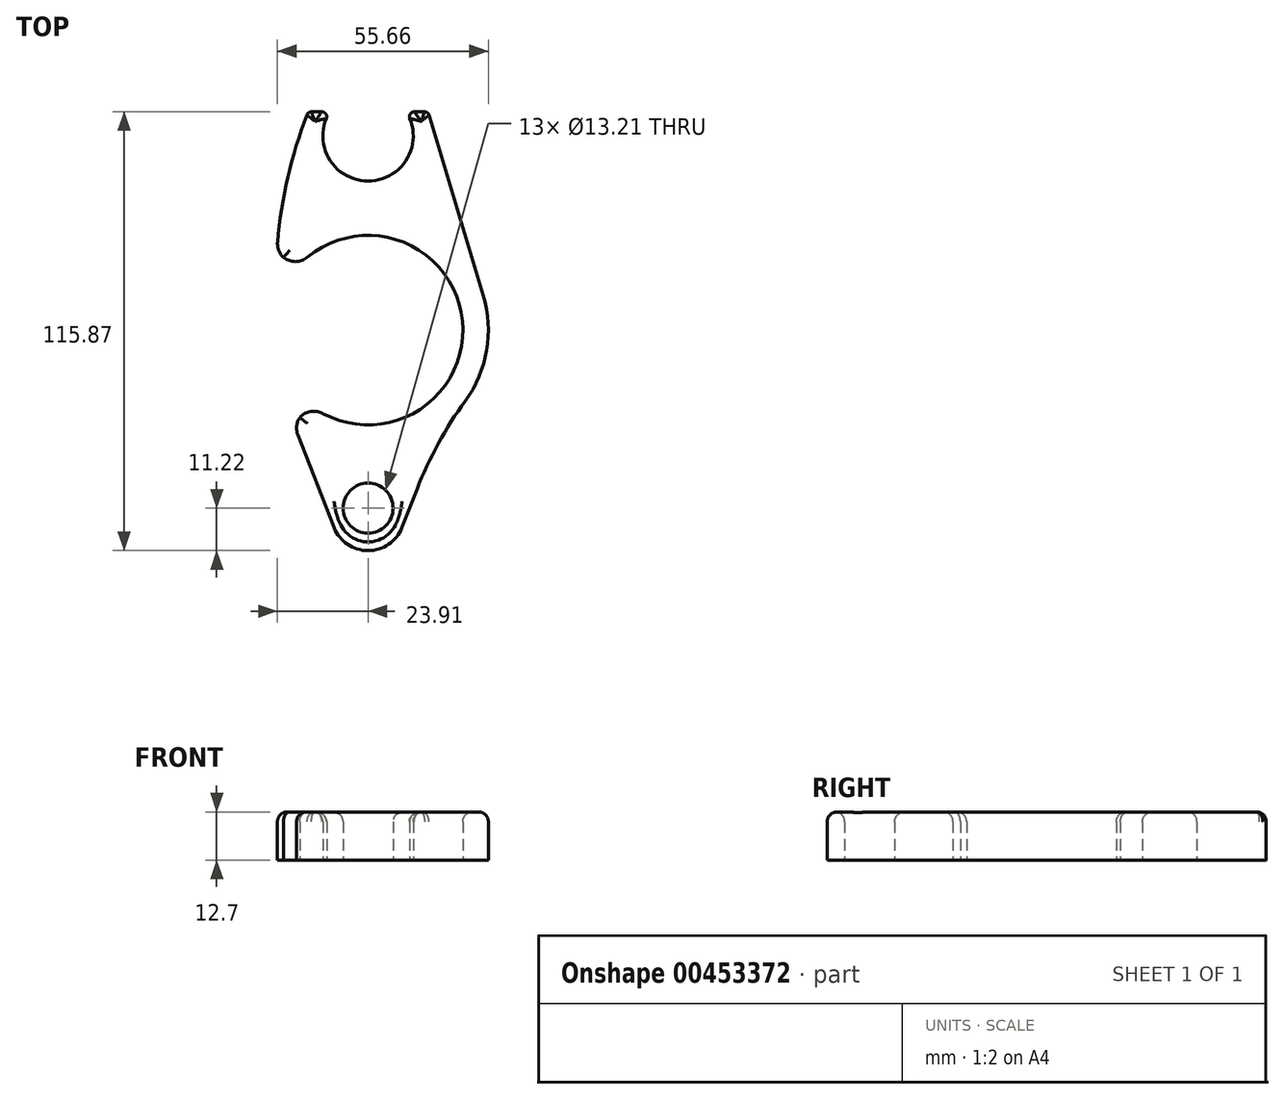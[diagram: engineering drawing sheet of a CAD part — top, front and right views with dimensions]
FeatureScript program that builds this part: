
annotation { "Feature Type Name" : "Feature", "Feature Type Description" : "" }
export const myFeature = defineFeature(function(context is Context, id is Id, definition is map)
    precondition{}
    {
        {
            var Q0;
            Q0=qCreatedBy(makeId("Top.planeOp"),FACE);
            var sketch = newSketch(context, id + "F0", { "sketchPlane" : qUnion([Q0])});
            skCircle(sketch, "E0", {"center": v(0, 0) * mm, "radius": 31.75 * mm});
            skCircle(sketch, "E1", {"center": v(0, -47) * mm, "radius": 6.6 * mm});
            skCircle(sketch, "E2", {"center": v(0, 51.3) * mm, "radius": 11.94 * mm});
            skCircle(sketch, "E3.0", {"center": v(0, 51.3) * mm, "radius": 17.02 * mm});
            skLineSegment(sketch, "E4", {"start": v(0, 57.66) * mm, "end": v(-15.79, 57.66) * mm});
            skLineSegment(sketch, "E5", {"start": v(-15.79, 57.66) * mm, "end": v(-26.07, 32.09) * mm});
            skLineSegment(sketch, "E6", {"start": v(-26.07, 32.09) * mm, "end": v(-22.42, 11.11) * mm});
            skLineSegment(sketch, "E7", {"start": v(0, 0) * mm, "end": v(0, 31.75) * mm, "construction": true});
            skLineSegment(sketch, "E8", {"start": v(0, 0) * mm, "end": v(-31.75, 0) * mm, "construction": true});
            skLineSegment(sketch, "E9", {"start": v(-22.42, -17.72) * mm, "end": v(0, -74.98) * mm});
            skLineSegment(sketch, "E10.MirrorCS", {"start": v(22.42, -17.72) * mm, "end": v(0, -74.98) * mm});
            skCircle(sketch, "E11", {"center": v(0, 0) * mm, "radius": 25.02 * mm});
            skLineSegment(sketch, "E12", {"start": v(16.3, 56.2) * mm, "end": v(30.41, 9.12) * mm});
            skLineSegment(sketch, "E13.MirrorCS", {"start": v(0, 57.66) * mm, "end": v(15.79, 57.66) * mm});
            skSolve(sketch);
        }
        {
            var Q0;
            {var subQ1=sQuery(id+"F0.wireOp",EDGE,"E5");Q0=makeQuery(id+"F0.imprint","IMPRINT",FACE,{"disambiguationData":[TD([[makeQuery(id+"F0.imprint","IMPRINT",EDGE,{"derivedFrom":subQ1}),1.0]])]});}
            var Q1;
            {var subQ0=sQuery(id+"F0.wireOp",EDGE,"E4");var subQ6=sQuery(id+"F0.wireOp",EDGE,"E2");var subQ7=makeQuery(id+"F0.imprint","INTERSECT",VERTEX,{"derivedFrom":[subQ6,subQ0]});Q1=makeQuery(id+"F0.imprint","IMPRINT",FACE,{"disambiguationData":[TD([[makeQuery(id+"F0.imprint","IMPRINT",EDGE,{"disambiguationData":[TD([[subQ7,-1.0]])],"derivedFrom":subQ6}),-1.0]])]});}
            var Q2;
            Q2=makeQuery(id+"F0.imprint","IMPRINT",FACE,{"disambiguationData":[TD([[makeQuery(id+"F0.imprint","IMPRINT",EDGE,{"derivedFrom":sQuery(id+"F0.wireOp",EDGE,"E1")}),-1.0]])]});
            var Q3;
            Q3=makeQuery(id+"F0.imprint","IMPRINT",FACE,{"disambiguationData":[TD([[makeQuery(id+"F0.imprint","IMPRINT",EDGE,{"derivedFrom":sQuery(id+"F0.wireOp",EDGE,"E11")}),-1.0]])]});
            extrude(context, id + "F1", {"entities" : qUnion([Q0, Q1, Q2, Q3]), "depth" : 12.7 * mm});
        }
        {
            var Q0;
            Q0=makeQuery(id+"F1.opExtrude","SWEPT_EDGE",EDGE,{"disambiguationData":[OSD([sQuery(id+"F0.wireOp",EDGE,"E9"),sQuery(id+"F0.wireOp",EDGE,"E10.MirrorCS")])]});
            fillet(context, id + "F2", {"entities" : qUnion([Q0]), "radius" : 9.62 * mm, "tangentPropagation" : true, "allowEdgeOverflow" : false});
        }
        {
            var Q0;
            Q0=makeQuery(id+"F1.opExtrude","CAP_FACE",FACE,{"disambiguationData":[OSD([sQuery(id+"F0.wireOp",EDGE,"E0"),sQuery(id+"F0.wireOp",EDGE,"E1"),sQuery(id+"F0.wireOp",EDGE,"E2"),sQuery(id+"F0.wireOp",EDGE,"E3.0"),sQuery(id+"F0.wireOp",EDGE,"E4"),sQuery(id+"F0.wireOp",EDGE,"E5"),sQuery(id+"F0.wireOp",EDGE,"E6"),sQuery(id+"F0.wireOp",EDGE,"E9"),sQuery(id+"F0.wireOp",EDGE,"E10.MirrorCS"),sQuery(id+"F0.wireOp",EDGE,"E11"),sQuery(id+"F0.wireOp",EDGE,"E12"),sQuery(id+"F0.wireOp",EDGE,"E13.MirrorCS")])],"isStart":false});
            var sketch = newSketch(context, id + "F3", { "sketchPlane" : qUnion([Q0])});
            skLineSegment(sketch, "E14", {"start": v(-24.09, 20.69) * mm, "end": v(0, 0) * mm});
            skLineSegment(sketch, "E15", {"start": v(0, 0) * mm, "end": v(-19.56, -25) * mm});
            skArc(sketch, "E16.0", {"start": v(-24.09, 20.69) * mm, "mid": v(-31.6, -3.13) * mm, "end": v(-19.56, -25) * mm});
            skSolve(sketch);
        }
        {
            var Q0;
            Q0 = qSketchRegion(id + "F3", true);
            extrude(context, id + "F4", {"entities" : qUnion([Q0]), "operationType" : NewBodyOperationType.REMOVE, "endBound" : BoundingType.THROUGH_ALL, "oppositeDirection" : true, "depth" : 25.4 * mm});
        }
        {
            var Q0;
            Q0=makeQuery(id+"F1.opExtrude","SWEPT_EDGE",EDGE,{"disambiguationData":[OSD([sQuery(id+"F0.wireOp",EDGE,"E5"),sQuery(id+"F0.wireOp",EDGE,"E6")])]});
            fillet(context, id + "F5", {"entities" : qUnion([Q0]), "radius" : 121.36 * mm, "tangentPropagation" : true, "allowEdgeOverflow" : false});
        }
        {
            var Q0;
            Q0=makeQuery(id+"F4.boolean.opBoolean","INTERSECT",EDGE,{"derivedFrom":[makeQuery(id+"F1.opExtrude","SWEPT_FACE",FACE,{"disambiguationData":[OSD([sQuery(id+"F0.wireOp",EDGE,"E11")])]}),makeQuery(id+"F4.opExtrude","SWEPT_FACE",FACE,{"disambiguationData":[OSD([sQuery(id+"F3.wireOp",EDGE,"E14")])]})]});
            var Q1;
            Q1=makeQuery(id+"F5.opFillet","BLEND_EDGE",EDGE,{"blendedFrom":[makeQuery(id+"F1.opExtrude","SWEPT_EDGE",EDGE,{"disambiguationData":[OSD([sQuery(id+"F0.wireOp",EDGE,"E5"),sQuery(id+"F0.wireOp",EDGE,"E6")])]}),makeQuery(id+"F4.boolean.opBoolean","COPY",FACE,{"derivedFrom":makeQuery(id+"F4.opExtrude","SWEPT_FACE",FACE,{"disambiguationData":[OSD([sQuery(id+"F3.wireOp",EDGE,"E14")])]})})],"blendedInto":[makeQuery(id+"F4.boolean.opBoolean","COPY",FACE,{"derivedFrom":makeQuery(id+"F4.opExtrude","SWEPT_FACE",FACE,{"disambiguationData":[OSD([sQuery(id+"F3.wireOp",EDGE,"E14")])]})})]});
            var Q2;
            Q2=makeQuery(id+"F4.boolean.opBoolean","INTERSECT",EDGE,{"derivedFrom":[makeQuery(id+"F1.opExtrude","SWEPT_FACE",FACE,{"disambiguationData":[OSD([sQuery(id+"F0.wireOp",EDGE,"E11")])]}),makeQuery(id+"F4.opExtrude","SWEPT_FACE",FACE,{"disambiguationData":[OSD([sQuery(id+"F3.wireOp",EDGE,"E15")])]})]});
            var Q3;
            {var subQ0=sQuery(id+"F0.wireOp",EDGE,"E9");Q3=makeQuery(id+"F4.boolean.opBoolean","MERGE",EDGE,{"derivedFrom":[makeQuery(id+"F1.opExtrude","SWEPT_EDGE",EDGE,{"disambiguationData":[OSD([sQuery(id+"F0.wireOp",EDGE,"E0"),subQ0])]}),makeQuery(id+"F4.opExtrude","SWEPT_EDGE",EDGE,{"disambiguationData":[OSD([subQ0,sQuery(id+"F3.wireOp",EDGE,"E15"),sQuery(id+"F3.wireOp",EDGE,"E16.0")])]})]});}
            fillet(context, id + "F6", {"entities" : qUnion([Q0, Q1, Q2, Q3]), "radius" : 5.08 * mm, "tangentPropagation" : true, "allowEdgeOverflow" : false});
        }
        {
            var Q0;
            Q0=makeQuery(id+"F1.opExtrude","SWEPT_EDGE",EDGE,{"disambiguationData":[OSD([sQuery(id+"F0.wireOp",EDGE,"E0"),sQuery(id+"F0.wireOp",EDGE,"E10.MirrorCS")])]});
            fillet(context, id + "F7", {"entities" : qUnion([Q0]), "radius" : 103.83 * mm, "tangentPropagation" : true, "allowEdgeOverflow" : false});
        }
        {
            var Q0;
            Q0=makeQuery(id+"F1.opExtrude","SWEPT_EDGE",EDGE,{"disambiguationData":[OSD([sQuery(id+"F0.wireOp",EDGE,"E3.0"),sQuery(id+"F0.wireOp",EDGE,"E13.MirrorCS")])]});
            var Q1;
            Q1=makeQuery(id+"F1.opExtrude","SWEPT_EDGE",EDGE,{"disambiguationData":[OSD([sQuery(id+"F0.wireOp",EDGE,"E2"),sQuery(id+"F0.wireOp",EDGE,"E13.MirrorCS")])]});
            var Q2;
            Q2=makeQuery(id+"F1.opExtrude","SWEPT_EDGE",EDGE,{"disambiguationData":[OSD([sQuery(id+"F0.wireOp",EDGE,"E2"),sQuery(id+"F0.wireOp",EDGE,"E4")])]});
            var Q3;
            Q3=makeQuery(id+"F5.opFillet","BLEND_EDGE",EDGE,{"blendedFrom":[makeQuery(id+"F1.opExtrude","SWEPT_EDGE",EDGE,{"disambiguationData":[OSD([sQuery(id+"F0.wireOp",EDGE,"E5"),sQuery(id+"F0.wireOp",EDGE,"E6")])]}),makeQuery(id+"F1.opExtrude","SWEPT_FACE",FACE,{"disambiguationData":[OSD([sQuery(id+"F0.wireOp",EDGE,"E4")])]})],"blendedInto":[makeQuery(id+"F1.opExtrude","SWEPT_FACE",FACE,{"disambiguationData":[OSD([sQuery(id+"F0.wireOp",EDGE,"E4")])]})]});
            fillet(context, id + "F8", {"entities" : qUnion([Q0, Q1, Q2, Q3]), "radius" : 1.27 * mm, "tangentPropagation" : true, "allowEdgeOverflow" : false});
        }
        {
            var Q0;
            Q0=makeQuery(id+"F1.opExtrude","CAP_FACE",FACE,{"disambiguationData":[OSD([sQuery(id+"F0.wireOp",EDGE,"E0"),sQuery(id+"F0.wireOp",EDGE,"E1"),sQuery(id+"F0.wireOp",EDGE,"E2"),sQuery(id+"F0.wireOp",EDGE,"E3.0"),sQuery(id+"F0.wireOp",EDGE,"E4"),sQuery(id+"F0.wireOp",EDGE,"E5"),sQuery(id+"F0.wireOp",EDGE,"E6"),sQuery(id+"F0.wireOp",EDGE,"E9"),sQuery(id+"F0.wireOp",EDGE,"E10.MirrorCS"),sQuery(id+"F0.wireOp",EDGE,"E11"),sQuery(id+"F0.wireOp",EDGE,"E12"),sQuery(id+"F0.wireOp",EDGE,"E13.MirrorCS")])],"isStart":false});
            fillet(context, id + "F9", {"entities" : qUnion([Q0]), "radius" : 2.54 * mm, "tangentPropagation" : true, "allowEdgeOverflow" : false});
        }
    });
